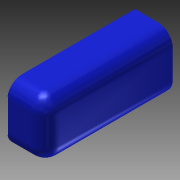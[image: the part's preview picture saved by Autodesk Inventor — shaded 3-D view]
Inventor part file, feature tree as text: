
AUTODESK INVENTOR PART (.ipt)
format: ipt  version: 2014 SP1 (Build 180222100, 222)  size: 183,808 bytes
history: native  units: in
note: dims shown in document units (in); Inventor stores cm internally (conversion verified against a paired STEP export)
features: reference x4, extrude x3, sketch x2, fillet x1, projected_geometry x1
ambient origin geometry x8: Origin, YZ Plane, XZ Plane, XY Plane, X Axis, Y Axis, Z Axis, Center Point
bodies: Solid1 (feature_tree)
feature tree (11):
  sketch  "Sketch1"  dims[d0=0.0625in d1=0.0in d3=1.0in]
  extrude  "Extrusion1"  Depth=1.0in
  extrude  "Extrusion2"  Depth=0.0625in
  extrude  "Extrusion3"  Depth=11.25in TaperAngle=0.0deg
  fillet  "Fillet1"  Radius=0.0625in
  reference  "Reference4"
  reference  "Reference5"
  sketch  "Sketch2"  dims[d7=1.0in d9=0.0625in d10=11.25in d11=0.0in d12=0.0625in d13=0.0in d14=1.3125in d15=0.0625in d16=0.0625in]
  reference  "Reference6"
  projected_geometry  "Projected Loop1"
  reference  "Reference7"
